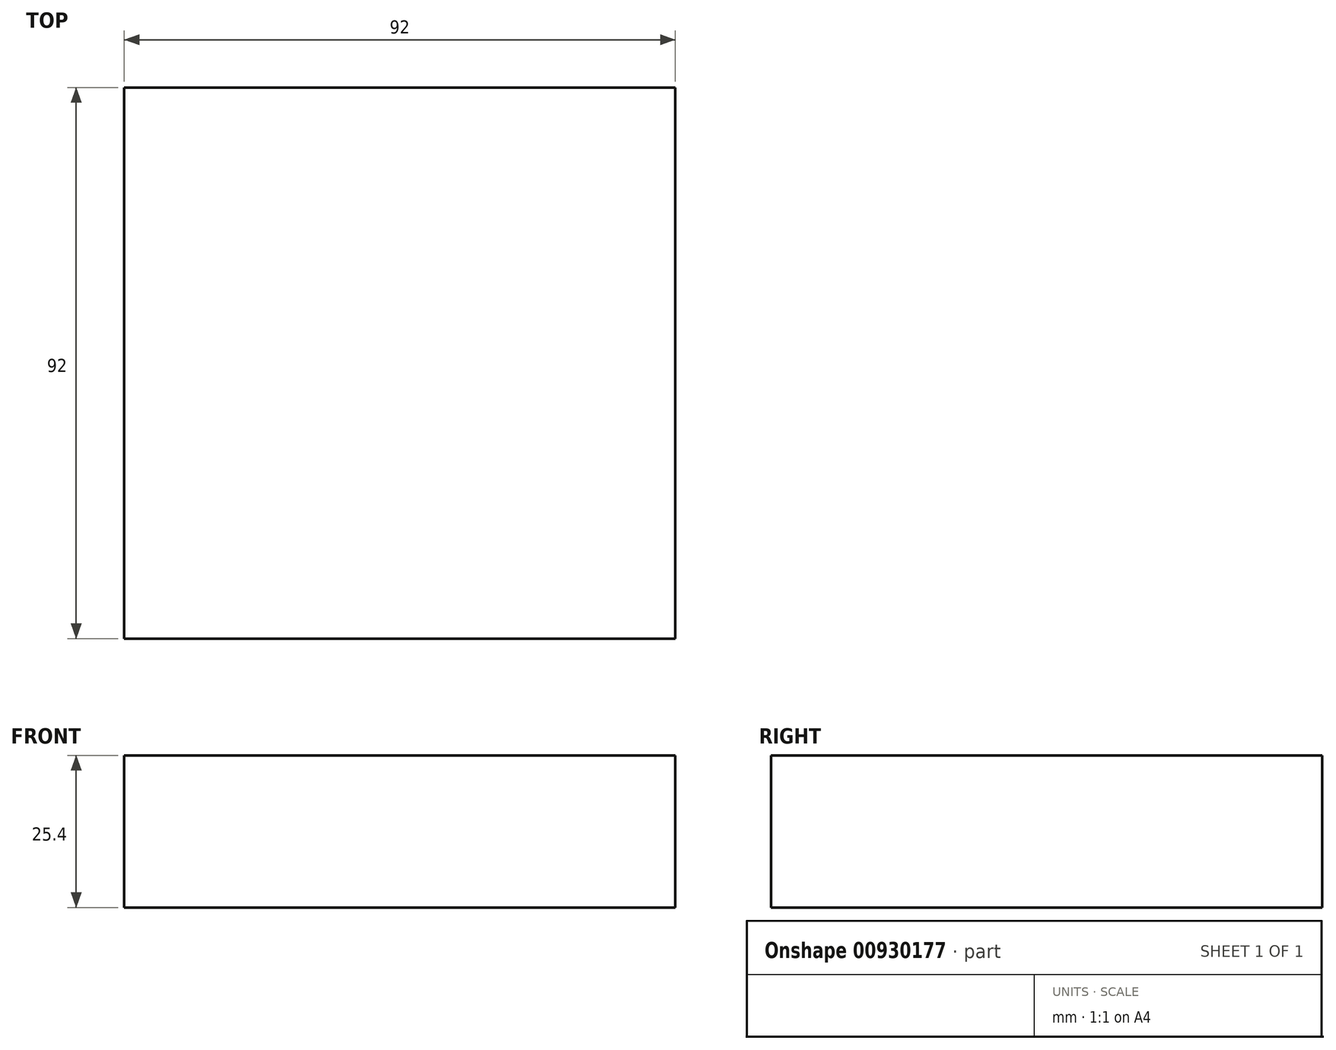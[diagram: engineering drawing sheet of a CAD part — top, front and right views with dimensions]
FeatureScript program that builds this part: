
annotation { "Feature Type Name" : "Feature", "Feature Type Description" : "" }
export const myFeature = defineFeature(function(context is Context, id is Id, definition is map)
    precondition{}
    {
        {
            var Q0;
            Q0=qCreatedBy(makeId("Top.planeOp"),FACE);
            var sketch = newSketch(context, id + "F0", { "sketchPlane" : qUnion([Q0])});
            skLineSegment(sketch, "E0.bottom", {"start": v(0, 0) * mm, "end": v(92, 0) * mm});
            skLineSegment(sketch, "E0.top", {"start": v(0, -92) * mm, "end": v(92, -92) * mm});
            skLineSegment(sketch, "E0.left", {"start": v(0, 0) * mm, "end": v(0, -92) * mm});
            skLineSegment(sketch, "E0.right", {"start": v(92, 0) * mm, "end": v(92, -92) * mm});
            skSolve(sketch);
        }
        {
            var Q0;
            Q0 = qSketchRegion(id + "F0", true);
            extrude(context, id + "F1", {"entities" : qUnion([Q0]), "depth" : 25.4 * mm, "offsetDistance" : 25.4 * mm});
        }
    });
